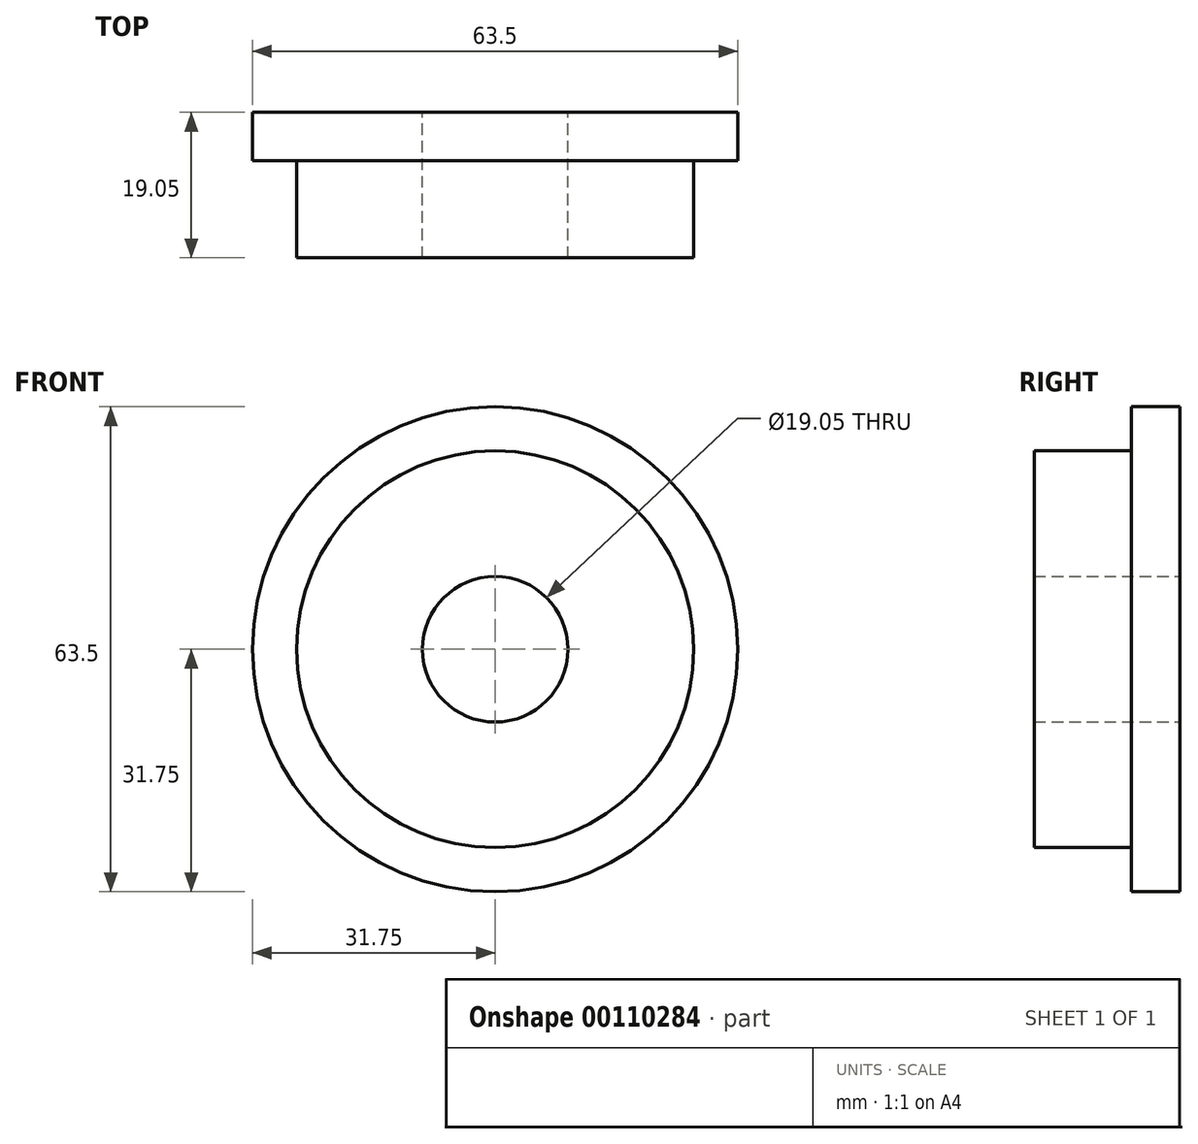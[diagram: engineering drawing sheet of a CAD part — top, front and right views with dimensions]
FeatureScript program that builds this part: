
annotation { "Feature Type Name" : "Feature", "Feature Type Description" : "" }
export const myFeature = defineFeature(function(context is Context, id is Id, definition is map)
    precondition{}
    {
        {
            var Q0;
            Q0=qCreatedBy(makeId("Front.planeOp"),FACE);
            var sketch = newSketch(context, id + "F0", { "sketchPlane" : qUnion([Q0])});
            skCircle(sketch, "E0", {"center": v(0, 0) * mm, "radius": 25.97 * mm});
            skSolve(sketch);
        }
        {
            var Q0;
            Q0=makeQuery(id+"F0.imprint","IMPRINT",FACE,{"disambiguationData":[TD([[makeQuery(id+"F0.imprint","IMPRINT",EDGE,{"derivedFrom":sQuery(id+"F0.wireOp",EDGE,"E0")}),1.0]])]});
            extrude(context, id + "F1", {"entities" : qUnion([Q0]), "depth" : 12.7 * mm});
        }
        {
            var Q0;
            Q0=makeQuery(id+"F1.opExtrude","CAP_FACE",FACE,{"disambiguationData":[OSD([sQuery(id+"F0.wireOp",EDGE,"E0")])],"isStart":true});
            var sketch = newSketch(context, id + "F2", { "sketchPlane" : qUnion([Q0])});
            skCircle(sketch, "E1", {"center": v(0, 0) * mm, "radius": 31.75 * mm});
            skSolve(sketch);
        }
        {
            var Q0;
            Q0 = qSketchRegion(id + "F2", true);
            extrude(context, id + "F3", {"entities" : qUnion([Q0]), "operationType" : NewBodyOperationType.ADD, "depth" : 6.35 * mm});
        }
        {
            var Q0;
            Q0=makeQuery(id+"F3.opExtrude","CAP_FACE",FACE,{"disambiguationData":[OSD([sQuery(id+"F2.wireOp",EDGE,"E1")])],"isStart":false});
            var sketch = newSketch(context, id + "F4", { "sketchPlane" : qUnion([Q0])});
            skCircle(sketch, "E2", {"center": v(0, 0) * mm, "radius": 9.52 * mm});
            skSolve(sketch);
        }
        {
            var Q0;
            Q0 = qSketchRegion(id + "F4", true);
            var Q1;
            Q1=makeQuery(id+"F1.opExtrude","CAP_FACE",FACE,{"disambiguationData":[OSD([sQuery(id+"F0.wireOp",EDGE,"E0")])],"isStart":false});
            extrude(context, id + "F5", {"entities" : qUnion([Q0]), "operationType" : NewBodyOperationType.REMOVE, "endBound" : BoundingType.UP_TO_SURFACE, "oppositeDirection" : true, "endBoundEntityFace" : qUnion([Q1]), "depth" : 25.4 * mm});
        }
    });
